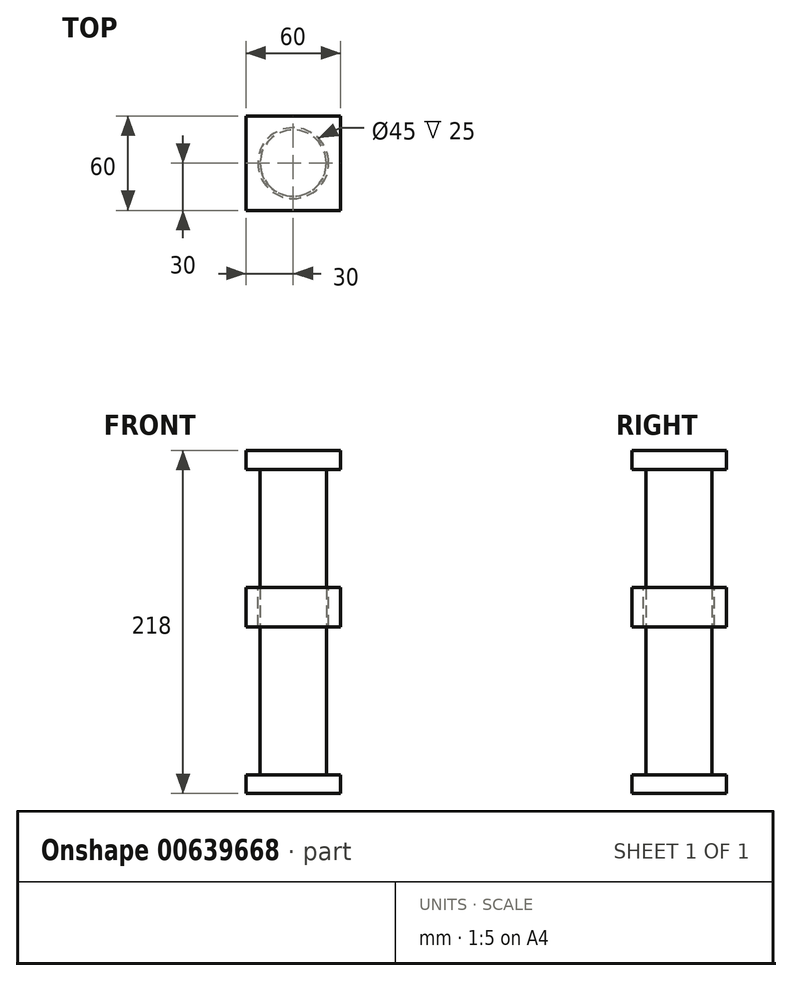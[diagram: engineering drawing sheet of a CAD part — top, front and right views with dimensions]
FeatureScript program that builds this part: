
annotation { "Feature Type Name" : "Feature", "Feature Type Description" : "" }
export const myFeature = defineFeature(function(context is Context, id is Id, definition is map)
    precondition{}
    {
        {
            var Q0;
            Q0=qCreatedBy(makeId("Top.planeOp"),FACE);
            var sketch = newSketch(context, id + "F0", { "sketchPlane" : qUnion([Q0])});
            skLineSegment(sketch, "E0.bottom", {"start": v(-30, 30) * mm, "end": v(30, 30) * mm});
            skLineSegment(sketch, "E0.top", {"start": v(-30, -30) * mm, "end": v(30, -30) * mm});
            skLineSegment(sketch, "E0.left", {"start": v(-30, 30) * mm, "end": v(-30, -30) * mm});
            skLineSegment(sketch, "E0.right", {"start": v(30, 30) * mm, "end": v(30, -30) * mm});
            skPoint(sketch, "E0.middle", {"position": v(0, 0) * mm});
            skSolve(sketch);
        }
        {
            var Q0;
            Q0=makeQuery(id+"F0.imprint","IMPRINT",FACE,{"disambiguationData":[TD([[makeQuery(id+"F0.imprint","IMPRINT",EDGE,{"derivedFrom":sQuery(id+"F0.wireOp",EDGE,"E0.bottom")}),-1.0]])]});
            extrude(context, id + "F1", {"entities" : qUnion([Q0]), "depth" : 25 * mm, "offsetDistance" : 25 * mm});
        }
        {
            var Q0;
            Q0=makeQuery(id+"F1.opExtrude","CAP_FACE",FACE,{"disambiguationData":[OSD([sQuery(id+"F0.wireOp",EDGE,"E0.bottom"),sQuery(id+"F0.wireOp",EDGE,"E0.top"),sQuery(id+"F0.wireOp",EDGE,"E0.left"),sQuery(id+"F0.wireOp",EDGE,"E0.right")])],"isStart":false});
            var sketch = newSketch(context, id + "F2", { "sketchPlane" : qUnion([Q0])});
            skCircle(sketch, "E1", {"center": v(0, 0) * mm, "radius": 22.5 * mm});
            skSolve(sketch);
        }
        {
            var Q0;
            Q0=makeQuery(id+"F2.imprint","IMPRINT",FACE,{"disambiguationData":[TD([[makeQuery(id+"F2.imprint","IMPRINT",EDGE,{"derivedFrom":sQuery(id+"F2.wireOp",EDGE,"E1")}),1.0]])]});
            extrude(context, id + "F3", {"entities" : qUnion([Q0]), "operationType" : NewBodyOperationType.REMOVE, "endBound" : BoundingType.THROUGH_ALL, "oppositeDirection" : true, "depth" : 25 * mm, "offsetDistance" : 25 * mm});
        }
        {
            var Q0;
            Q0=qCreatedBy(makeId("Top.planeOp"),FACE);
            var sketch = newSketch(context, id + "F4", { "sketchPlane" : qUnion([Q0])});
            skCircle(sketch, "E2", {"center": v(0, 0) * mm, "radius": 21 * mm});
            skSolve(sketch);
        }
        {
            var Q0;
            Q0=makeQuery(id+"F4.imprint","IMPRINT",FACE,{"disambiguationData":[TD([[makeQuery(id+"F4.imprint","IMPRINT",EDGE,{"derivedFrom":sQuery(id+"F4.wireOp",EDGE,"E2")}),1.0]])]});
            extrude(context, id + "F5", {"entities" : qUnion([Q0]), "endBound" : BoundingType.SYMMETRIC, "depth" : 200 * mm, "offsetDistance" : 25 * mm});
        }
        {
            var Q0;
            Q0=makeQuery(id+"F5.opExtrude","CAP_FACE",FACE,{"disambiguationData":[OSD([sQuery(id+"F4.wireOp",EDGE,"E2")])],"isStart":false});
            var sketch = newSketch(context, id + "F6", { "sketchPlane" : qUnion([Q0])});
            skLineSegment(sketch, "E3.bottom", {"start": v(-30, 30) * mm, "end": v(30, 30) * mm});
            skLineSegment(sketch, "E3.top", {"start": v(-30, -30) * mm, "end": v(30, -30) * mm});
            skLineSegment(sketch, "E3.left", {"start": v(-30, 30) * mm, "end": v(-30, -30) * mm});
            skLineSegment(sketch, "E3.right", {"start": v(30, 30) * mm, "end": v(30, -30) * mm});
            skPoint(sketch, "E3.middle", {"position": v(0, 0) * mm});
            skSolve(sketch);
        }
        {
            var Q0;
            Q0=makeQuery(id+"F5.opExtrude","CAP_FACE",FACE,{"disambiguationData":[OSD([sQuery(id+"F4.wireOp",EDGE,"E2")])],"isStart":true});
            var sketch = newSketch(context, id + "F7", { "sketchPlane" : qUnion([Q0])});
            skLineSegment(sketch, "E4.bottom", {"start": v(30, -30) * mm, "end": v(-30, -30) * mm});
            skLineSegment(sketch, "E4.top", {"start": v(30, 30) * mm, "end": v(-30, 30) * mm});
            skLineSegment(sketch, "E4.left", {"start": v(30, -30) * mm, "end": v(30, 30) * mm});
            skLineSegment(sketch, "E4.right", {"start": v(-30, -30) * mm, "end": v(-30, 30) * mm});
            skPoint(sketch, "E4.middle", {"position": v(0, 0) * mm});
            skSolve(sketch);
        }
        {
            var Q0;
            Q0=makeQuery(id+"F7.imprint","IMPRINT",FACE,{"disambiguationData":[TD([[makeQuery(id+"F7.imprint","IMPRINT",EDGE,{"derivedFrom":sQuery(id+"F7.wireOp",EDGE,"E4.bottom")}),-1.0]])]});
            var Q1;
            Q1=makeQuery(id+"F7.imprint","IMPRINT",FACE,{"disambiguationData":[TD([[makeQuery(id+"F7.imprint","IMPRINT",EDGE,{"derivedFrom":makeQuery(id+"F5.opExtrude","CAP_EDGE",EDGE,{"disambiguationData":[OSD([sQuery(id+"F4.wireOp",EDGE,"E2")])],"isStart":true})}),-1.0]])]});
            extrude(context, id + "F8", {"entities" : qUnion([Q0, Q1]), "operationType" : NewBodyOperationType.ADD, "endBound" : BoundingType.SYMMETRIC, "depth" : 12 * mm, "offsetDistance" : 25 * mm});
        }
        {
            var Q0;
            Q0 = qSketchRegion(id + "F6", true);
            extrude(context, id + "F9", {"entities" : qUnion([Q0]), "operationType" : NewBodyOperationType.ADD, "depth" : 12 * mm, "offsetDistance" : 25 * mm});
        }
    });
